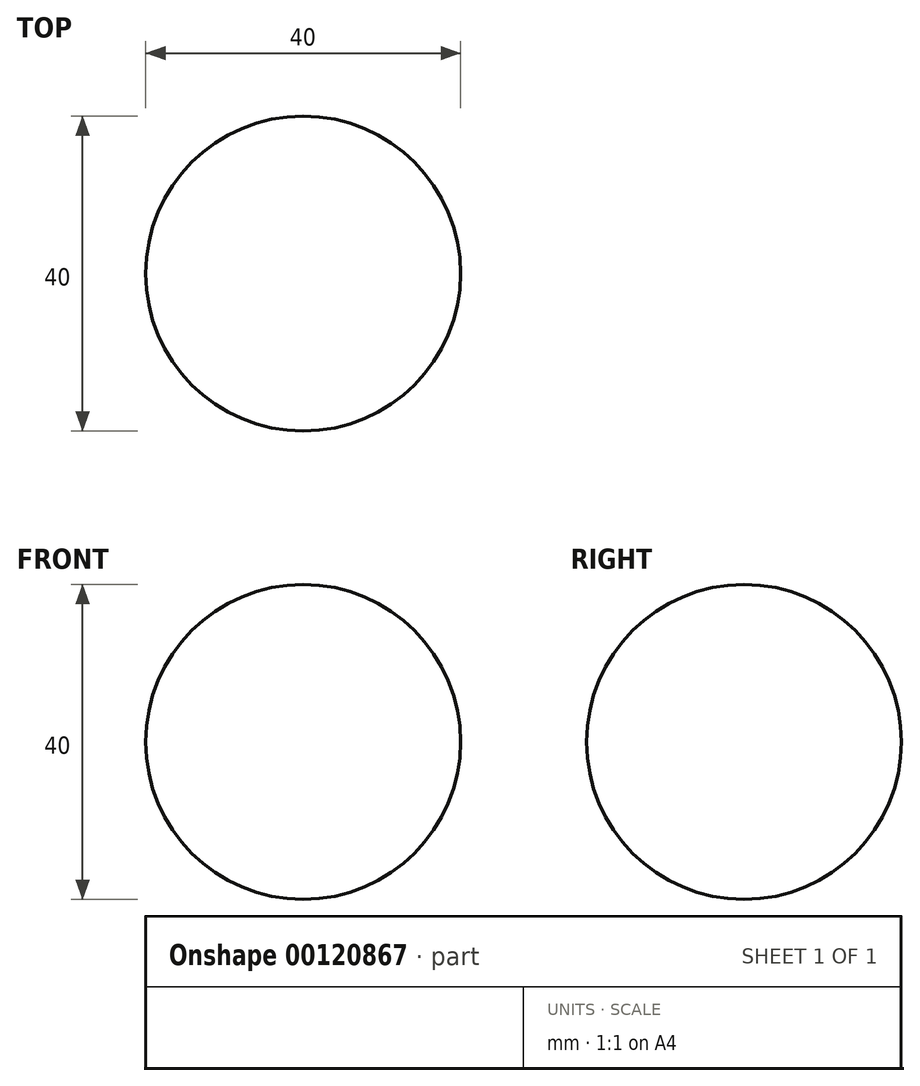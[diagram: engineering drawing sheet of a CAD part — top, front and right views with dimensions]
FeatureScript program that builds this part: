
annotation { "Feature Type Name" : "Feature", "Feature Type Description" : "" }
export const myFeature = defineFeature(function(context is Context, id is Id, definition is map)
    precondition{}
    {
        {
            var Q0;
            Q0=qCreatedBy(makeId("Front.planeOp"),FACE);
            var sketch = newSketch(context, id + "F0", { "sketchPlane" : qUnion([Q0])});
            skArc(sketch, "E0", {"start": v(20, 0) * mm, "mid": v(0, 20) * mm, "end": v(-20, 0) * mm});
            skLineSegment(sketch, "E1", {"start": v(-20, 0) * mm, "end": v(20, 0) * mm});
            skSolve(sketch);
        }
        {
            var Q0;
            Q0=makeQuery(id+"F0.imprint","IMPRINT",FACE,{"disambiguationData":[TD([[makeQuery(id+"F0.imprint","IMPRINT",EDGE,{"derivedFrom":sQuery(id+"F0.wireOp",EDGE,"E0")}),1.0]])]});
            var Q1;
            Q1=sQuery(id+"F0.wireOp",EDGE,"E1");
            revolve(context, id + "F1", {"entities" : qUnion([Q0]), "axis" : qUnion([Q1]), "revolveType" : RevolveType.FULL});
        }
    });
